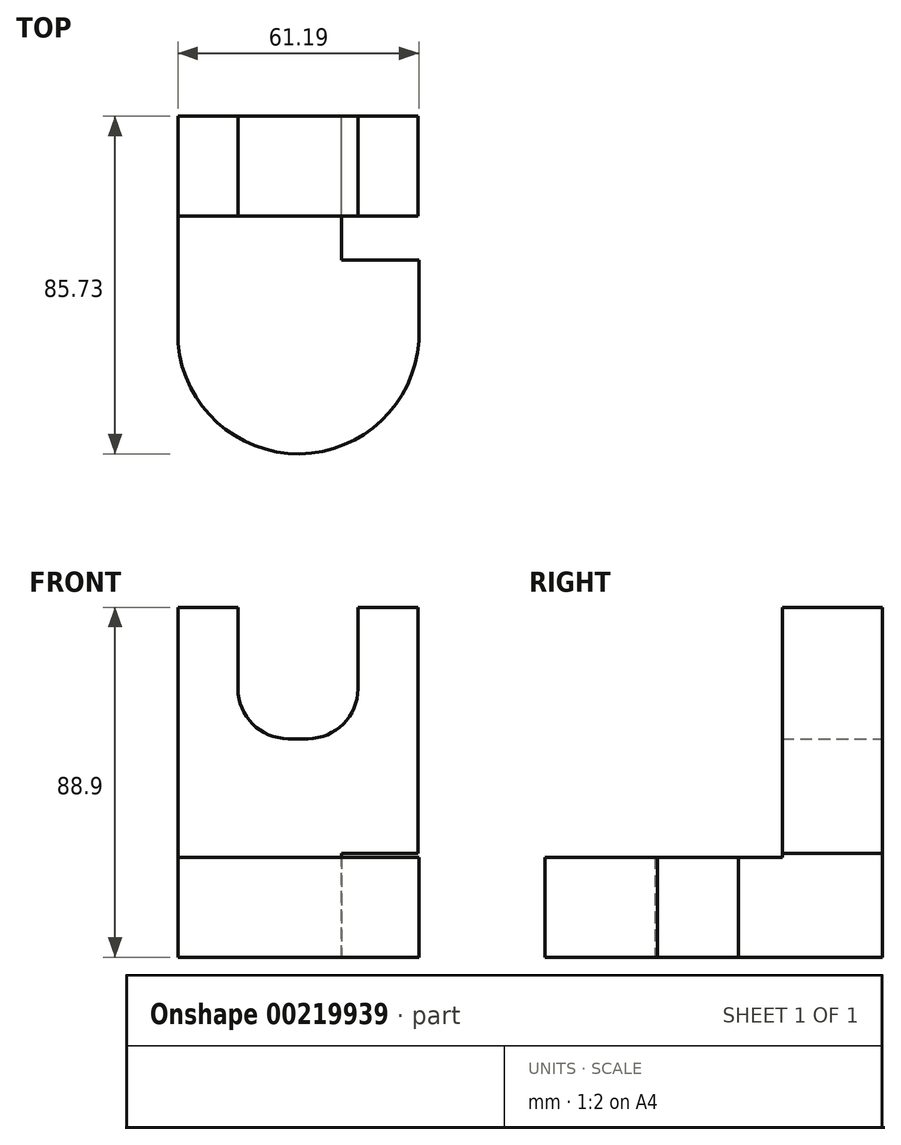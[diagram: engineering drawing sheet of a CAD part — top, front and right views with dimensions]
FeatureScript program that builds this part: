
annotation { "Feature Type Name" : "Feature", "Feature Type Description" : "" }
export const myFeature = defineFeature(function(context is Context, id is Id, definition is map)
    precondition{}
    {
        {
            var Q0;
            Q0=qCreatedBy(makeId("Front.planeOp"),FACE);
            var sketch = newSketch(context, id + "F0", { "sketchPlane" : qUnion([Q0])});
            skLineSegment(sketch, "E0.top", {"start": v(-28.17, -33.37) * mm, "end": v(13.4, -33.37) * mm});
            skLineSegment(sketch, "E0.left", {"start": v(-28.17, 55.53) * mm, "end": v(-28.17, -33.37) * mm});
            skLineSegment(sketch, "E0.right", {"start": v(32.79, 55.53) * mm, "end": v(32.79, -7.04) * mm});
            skLineSegment(sketch, "E1", {"start": v(-28.17, 55.53) * mm, "end": v(-12.93, 55.53) * mm});
            skLineSegment(sketch, "E2", {"start": v(32.79, 55.53) * mm, "end": v(17.55, 55.53) * mm});
            skLineSegment(sketch, "E3", {"start": v(-12.93, 55.53) * mm, "end": v(-12.93, 34.84) * mm});
            skPoint(sketch, "E4.start.orphan", {"position": v(17.55, 55.53) * mm});
            skLineSegment(sketch, "E5", {"start": v(17.55, 55.53) * mm, "end": v(17.55, 34.84) * mm});
            skLineSegment(sketch, "E6", {"start": v(4.85, 22.14) * mm, "end": v(-0.23, 22.14) * mm});
            skPoint(sketch, "E7.orphan", {"position": v(2.3, 55.53) * mm});
            skPoint(sketch, "E8.visualSharp", {"position": v(-12.93, 22.14) * mm});
            skArc(sketch, "E8.filletArc", {"start": v(-12.93, 34.84) * mm, "mid": v(-9.21, 25.86) * mm, "end": v(-0.23, 22.14) * mm});
            skPoint(sketch, "E9.visualSharp", {"position": v(17.55, 22.14) * mm});
            skArc(sketch, "E9.filletArc", {"start": v(4.85, 22.14) * mm, "mid": v(13.83, 25.86) * mm, "end": v(17.55, 34.84) * mm});
            skLineSegment(sketch, "E10.top", {"start": v(13.4, -7.04) * mm, "end": v(32.79, -7.04) * mm});
            skLineSegment(sketch, "E10.left", {"start": v(13.4, -33.37) * mm, "end": v(13.4, -7.04) * mm});
            skSolve(sketch);
        }
        {
            var Q0;
            Q0 = qSketchRegion(id + "F0", true);
            extrude(context, id + "F1", {"entities" : qUnion([Q0]), "depth" : 25.4 * mm});
        }
        {
            var Q0;
            Q0=makeQuery(id+"F1.opExtrude","SWEPT_FACE",FACE,{"disambiguationData":[OSD([sQuery(id+"F0.wireOp",EDGE,"E0.top")])]});
            var sketch = newSketch(context, id + "F2", { "sketchPlane" : qUnion([Q0])});
            skLineSegment(sketch, "E11.bottom", {"start": v(-28.17, 0) * mm, "end": v(13.4, 0) * mm});
            skLineSegment(sketch, "E11.left", {"start": v(-28.17, 0) * mm, "end": v(-28.17, 57.72) * mm});
            skLineSegment(sketch, "E11.right", {"start": v(33.02, 36.53) * mm, "end": v(33.02, 57.06) * mm});
            skArc(sketch, "E12", {"start": v(33.02, 57.06) * mm, "mid": v(2.73, 85.73) * mm, "end": v(-28.17, 57.72) * mm});
            skLineSegment(sketch, "E13", {"start": v(13.4, 0) * mm, "end": v(13.4, 36.53) * mm});
            skLineSegment(sketch, "E14", {"start": v(13.4, 36.53) * mm, "end": v(33.02, 36.53) * mm});
            skSolve(sketch);
        }
        {
            var Q0;
            Q0 = qSketchRegion(id + "F2", true);
            extrude(context, id + "F3", {"entities" : qUnion([Q0]), "operationType" : NewBodyOperationType.ADD, "oppositeDirection" : true, "depth" : 25.4 * mm});
        }
    });
